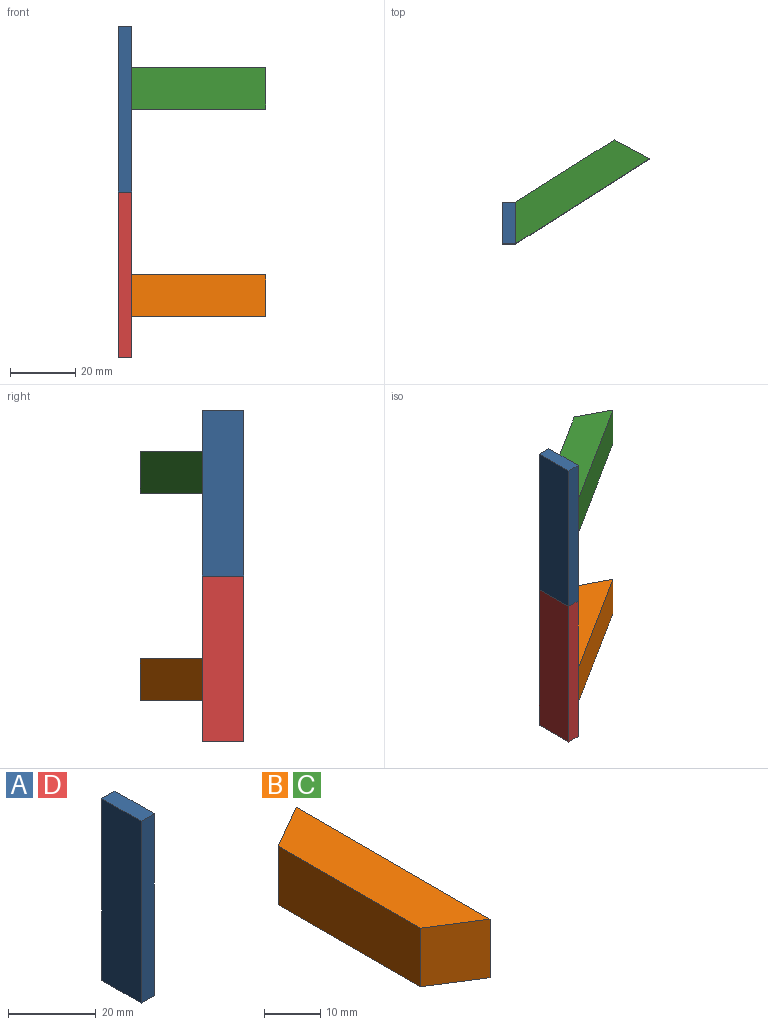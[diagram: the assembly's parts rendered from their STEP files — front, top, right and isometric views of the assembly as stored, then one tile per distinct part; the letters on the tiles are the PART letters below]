
ASSEMBLY  parts=4 mates=3
PART A: 6 faces, bbox 4.2x12.7x50.8 mm
  f0: plane 12.7x4.22mm, normal (0,0,1), area 53.5mm2, adj f1,f3,f4,f5
  f1: plane 50.8x12.7mm, normal (-1,0,0), area 645.2mm2, adj f0,f2,f4,f5
  f2: plane 12.7x4.22mm, normal (0,0,-1), area 53.5mm2, adj f1,f3,f4,f5
  f3: plane 50.8x12.7mm, normal (1,0,0), area 645.2mm2, adj f0,f2,f4,f5
  f4: plane 50.8x4.22mm, normal (0,-1,0), area 214.2mm2, adj f0,f1,f2,f3
  f5: plane 50.8x4.22mm, normal (0,1,0), area 214.2mm2, adj f0,f1,f2,f3
PART B: 6 faces, bbox 10.7x48.6x12.7 mm
  f0: plane 48.55x12.7mm, normal (1,0,0), area 616.6mm2, adj f1,f3,f4,f5
  f1: plane 12.7x10.73mm, normal (-0.5,0.87,0), area 157.3mm2, adj f0,f2,f4,f5
  f2: plane 35.56x12.7mm, normal (-1,0,0), area 451.6mm2, adj f1,f3,f4,f5
  f3: plane 12.7x10.73mm, normal (-0.54,-0.84,0), area 161.3mm2, adj f0,f2,f4,f5
  f4: plane 48.55x10.73mm, normal (0,0,1), area 451.2mm2, adj f0,f1,f2,f3
  f5: plane 48.55x10.73mm, normal (0,0,-1), area 451.2mm2, adj f0,f1,f2,f3
PART C: same geometry as B
PART D: same geometry as A
PLACE A t=(-27.51,0,50.99)mm
PLACE B rot(axis=(0,0,-1),57.6deg) t=(18.4,0.29,-12.51)mm
PLACE C rot(axis=(0,0,-1),57.6deg) t=(18.4,0.29,50.99)mm
PLACE D t=(-27.51,0,0.19)mm
MATE fastened B.f3 <-> D.f3  axis (-1,0,0) through (-2.11,-12.7,0.19)mm
MATE fastened A.f2 <-> D.f0  axis (0,0,-1) through (-4.21,-6.35,25.59)mm
MATE fastened C.f3 <-> A.f3  axis (-1,0,0) through (-2.11,-12.7,50.99)mm
